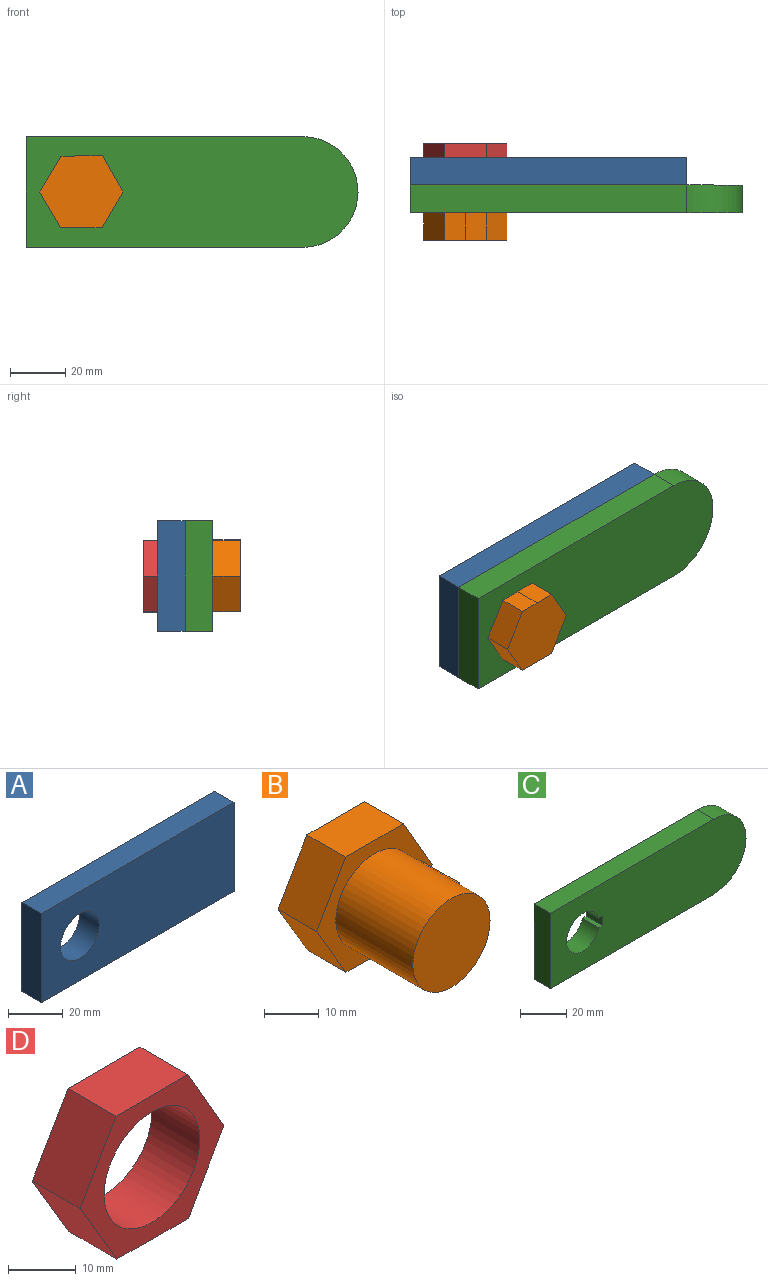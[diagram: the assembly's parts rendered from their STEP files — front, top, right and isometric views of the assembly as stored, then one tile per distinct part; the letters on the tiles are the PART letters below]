
ASSEMBLY  parts=4 mates=3
PART A: 7 faces, bbox 100x10x40 mm
  f0: plane 100x10mm, normal (0,0,1), area 1000mm2, adj f1,f4,f5,f6
  f1: plane 40x10mm, normal (-1,0,0), area 400mm2, adj f0,f2,f5,f6
  f2: plane 100x10mm, normal (0,0,-1), area 1000mm2, adj f1,f4,f5,f6
  f3: cylinder r=10mm len=20mm, axis (0,1,0), area 628.3mm2, adj f5,f6
  f4: plane 40x10mm, normal (1,0,0), area 400mm2, adj f0,f2,f5,f6
  f5: plane 100x40mm, normal (0,-1,0), area 3685.8mm2, adj f0,f1,f2,f3,f4
  f6: plane 100x40mm, normal (0,1,0), area 3685.8mm2, adj f0,f1,f2,f3,f4
PART B: 15 faces, bbox 30x30x26.1 mm
  f0: cylinder r=10mm len=20mm, axis (0,1,0), area 1206.1mm2, adj f1,f10,f11,f12,f14
  f1: plane 20x20mm, normal (0,-1,0), area 314.2mm2, adj f0
  f2: plane 30x26.05mm, normal (0,1,0), area 585.1mm2, adj f3,f4,f5,f6,f7,f8,f9
  f3: plane 13.06x10mm, normal (0.87,0,-0.49), area 150mm2, adj f2,f4,f9,f10
  f4: plane 12.99x10mm, normal (0.87,0,0.5), area 150mm2, adj f2,f3,f5,f10
  f5: plane 15x10mm, normal (0,0,1), area 150mm2, adj f2,f4,f6,f10
  f6: plane 12.99x10mm, normal (-0.87,0,0.5), area 150mm2, adj f2,f5,f7,f10
  f7: plane 12.91x10mm, normal (-0.86,0,-0.51), area 150mm2, adj f2,f6,f8,f10
  f8: plane 10x7.5mm, normal (-0.02,0,-1), area 75mm2, adj f2,f7,f9,f10
  f9: plane 10x7.5mm, normal (0,0,-1), area 75mm2, adj f2,f3,f8,f10
  f10: plane 30x26.05mm, normal (0,-1,0), area 260.4mm2, adj f0,f3,f4,f5,f6,f7,f8,f9
  f11: plane 5x2.32mm, normal (0,-1,0), area 10.5mm2, adj f0,f12,f13,f14
  f12: plane 10x2.32mm, normal (0,0,-1), area 23.2mm2, adj f0,f10,f11,f13
  f13: plane 10x5mm, normal (1,0,0), area 50mm2, adj f10,f11,f12,f14
  f14: plane 10x2.32mm, normal (0,0,1), area 23.2mm2, adj f0,f10,f11,f13
PART C: 10 faces, bbox 120x10x40 mm
  f0: cylinder r=20mm len=40mm, axis (0,1,0), area 628.3mm2, adj f1,f7,f8,f9
  f1: plane 100x10mm, normal (0,0,1), area 1000mm2, adj f0,f2,f8,f9
  f2: plane 40x10mm, normal (-1,0,0), area 400mm2, adj f1,f7,f8,f9
  f3: cylinder r=10mm len=20mm, axis (0,1,0), area 577.8mm2, adj f4,f6,f8,f9
  f4: plane 10x2.32mm, normal (0,0,-1), area 23.2mm2, adj f3,f5,f8,f9
  f5: plane 10x5mm, normal (-1,0,0), area 50mm2, adj f4,f6,f8,f9
  f6: plane 10x2.32mm, normal (0,0,1), area 23.2mm2, adj f3,f5,f8,f9
  f7: plane 100x10mm, normal (0,0,-1), area 1000mm2, adj f0,f2,f8,f9
  f8: plane 120x40mm, normal (0,-1,0), area 4303.6mm2, adj f0,f1,f2,f3,f4,f5,f6,f7
  f9: plane 120x40mm, normal (0,1,0), area 4303.6mm2, adj f0,f1,f2,f3,f4,f5,f6,f7
PART D: 10 faces, bbox 30x10x26.1 mm
  f0: plane 13.06x10mm, normal (0.87,0,-0.49), area 150mm2, adj f1,f7,f8,f9
  f1: plane 12.99x10mm, normal (0.87,0,0.5), area 150mm2, adj f0,f2,f8,f9
  f2: plane 15x10mm, normal (0,0,1), area 150mm2, adj f1,f3,f8,f9
  f3: plane 12.99x10mm, normal (-0.87,0,0.5), area 150mm2, adj f2,f4,f8,f9
  f4: plane 12.91x10mm, normal (-0.86,0,-0.51), area 150mm2, adj f3,f5,f8,f9
  f5: plane 10x7.5mm, normal (-0.02,0,-1), area 75mm2, adj f4,f7,f8,f9
  f6: cylinder r=10mm len=20mm, axis (0,1,0), area 628.3mm2, adj f8,f9
  f7: plane 10x7.5mm, normal (0,0,-1), area 75mm2, adj f0,f5,f8,f9
  f8: plane 30x26.05mm, normal (0,-1,0), area 270.9mm2, adj f0,f1,f2,f3,f4,f5,f6,f7
  f9: plane 30x26.05mm, normal (0,1,0), area 270.9mm2, adj f0,f1,f2,f3,f4,f5,f6,f7
PLACE A rot(axis=(0.09,-1,0),0deg) t=(72.03,162.73,-60.66)mm fixed
PLACE B rot(axis=(-1,0,0),180deg) t=(72.03,132.73,-60.66)mm
PLACE C t=(72.03,152.73,-60.66)mm
PLACE D t=(72.03,167.73,-60.66)mm
MATE revolute B.f0 <-> C.f3  axis (0,-1,0) through (72.03,142.73,-60.66)mm
MATE fastened A.f3 <-> B.f0  axis (0,1,0) through (72.03,162.73,-60.66)mm
MATE fastened B.f0 <-> D.f6  axis (0,1,0) through (72.03,162.73,-60.66)mm
